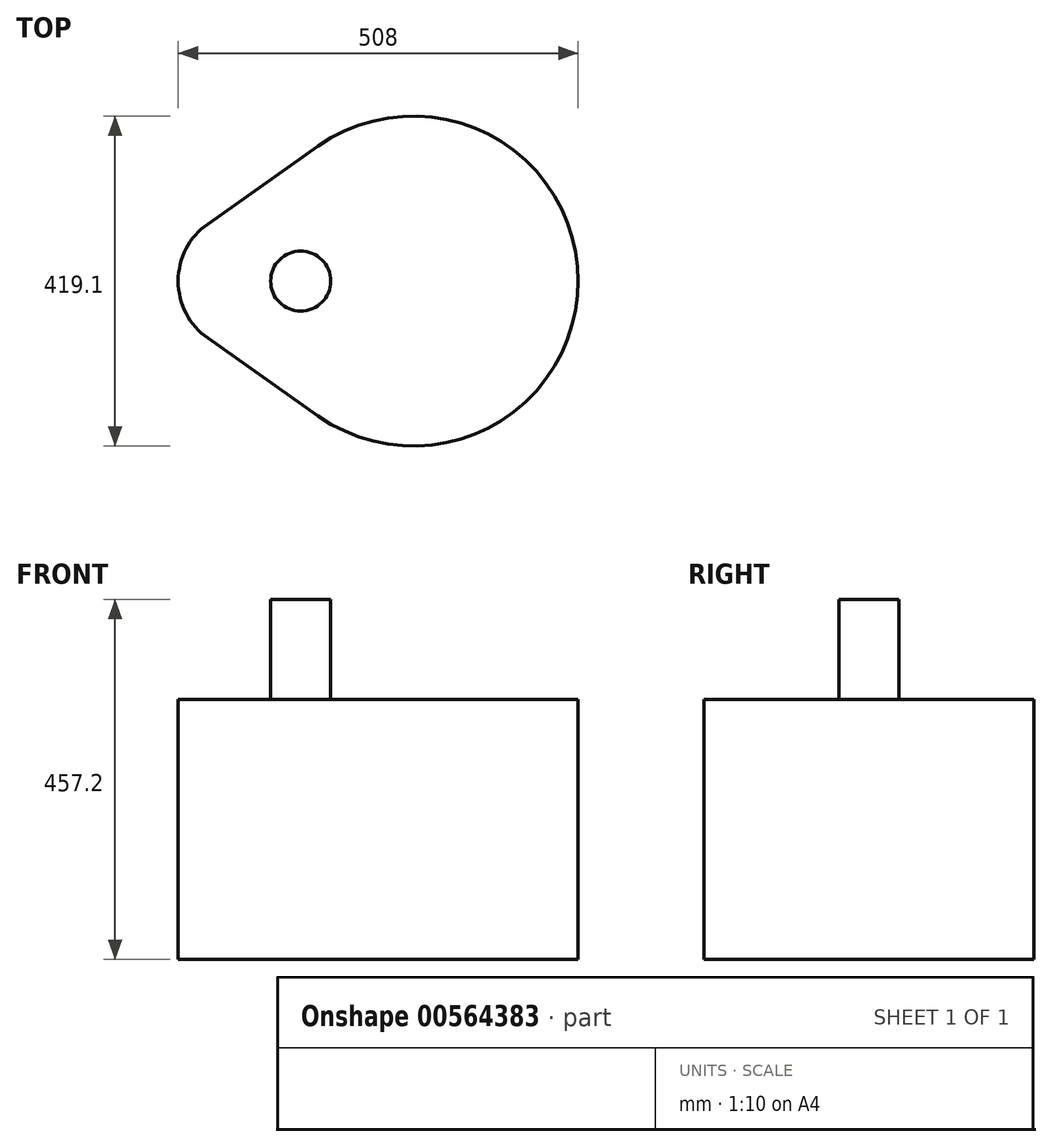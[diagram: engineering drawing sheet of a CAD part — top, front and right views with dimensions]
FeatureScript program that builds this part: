
annotation { "Feature Type Name" : "Feature", "Feature Type Description" : "" }
export const myFeature = defineFeature(function(context is Context, id is Id, definition is map)
    precondition{}
    {
        {
            var Q0;
            Q0=qCreatedBy(makeId("Top.planeOp"),FACE);
            var sketch = newSketch(context, id + "F0", { "sketchPlane" : qUnion([Q0])});
            skArc(sketch, "E0", {"start": v(-76.2, -171.33) * mm, "mid": v(254, 0) * mm, "end": v(-76.2, 171.33) * mm});
            skArc(sketch, "E1", {"start": v(-216.28, 72.69) * mm, "mid": v(-254, 0) * mm, "end": v(-216.28, -72.69) * mm});
            skLineSegment(sketch, "E2", {"start": v(-216.28, 72.69) * mm, "end": v(-76.2, 171.33) * mm});
            skLineSegment(sketch, "E3", {"start": v(-216.28, -72.69) * mm, "end": v(-76.2, -171.33) * mm});
            skLineSegment(sketch, "E4", {"start": v(-254, 0) * mm, "end": v(254, 0) * mm, "construction": true});
            skSolve(sketch);
        }
        {
            var Q0;
            Q0 = qSketchRegion(id + "F0", true);
            extrude(context, id + "F1", {"entities" : qUnion([Q0]), "depth" : 330.2 * mm, "offsetDistance" : 25.4 * mm});
        }
        {
            var Q0;
            Q0=makeQuery(id+"F1.opExtrude","CAP_FACE",FACE,{"disambiguationData":[OSD([sQuery(id+"F0.wireOp",EDGE,"E0"),sQuery(id+"F0.wireOp",EDGE,"E1"),sQuery(id+"F0.wireOp",EDGE,"E2"),sQuery(id+"F0.wireOp",EDGE,"E3")])],"isStart":false});
            var sketch = newSketch(context, id + "F2", { "sketchPlane" : qUnion([Q0])});
            skCircle(sketch, "E5", {"center": v(-98.42, 0) * mm, "radius": 38.1 * mm});
            skSolve(sketch);
        }
        {
            var Q0;
            Q0 = qSketchRegion(id + "F2", true);
            extrude(context, id + "F3", {"entities" : qUnion([Q0]), "operationType" : NewBodyOperationType.ADD, "depth" : 127 * mm, "offsetDistance" : 25.4 * mm});
        }
    });
